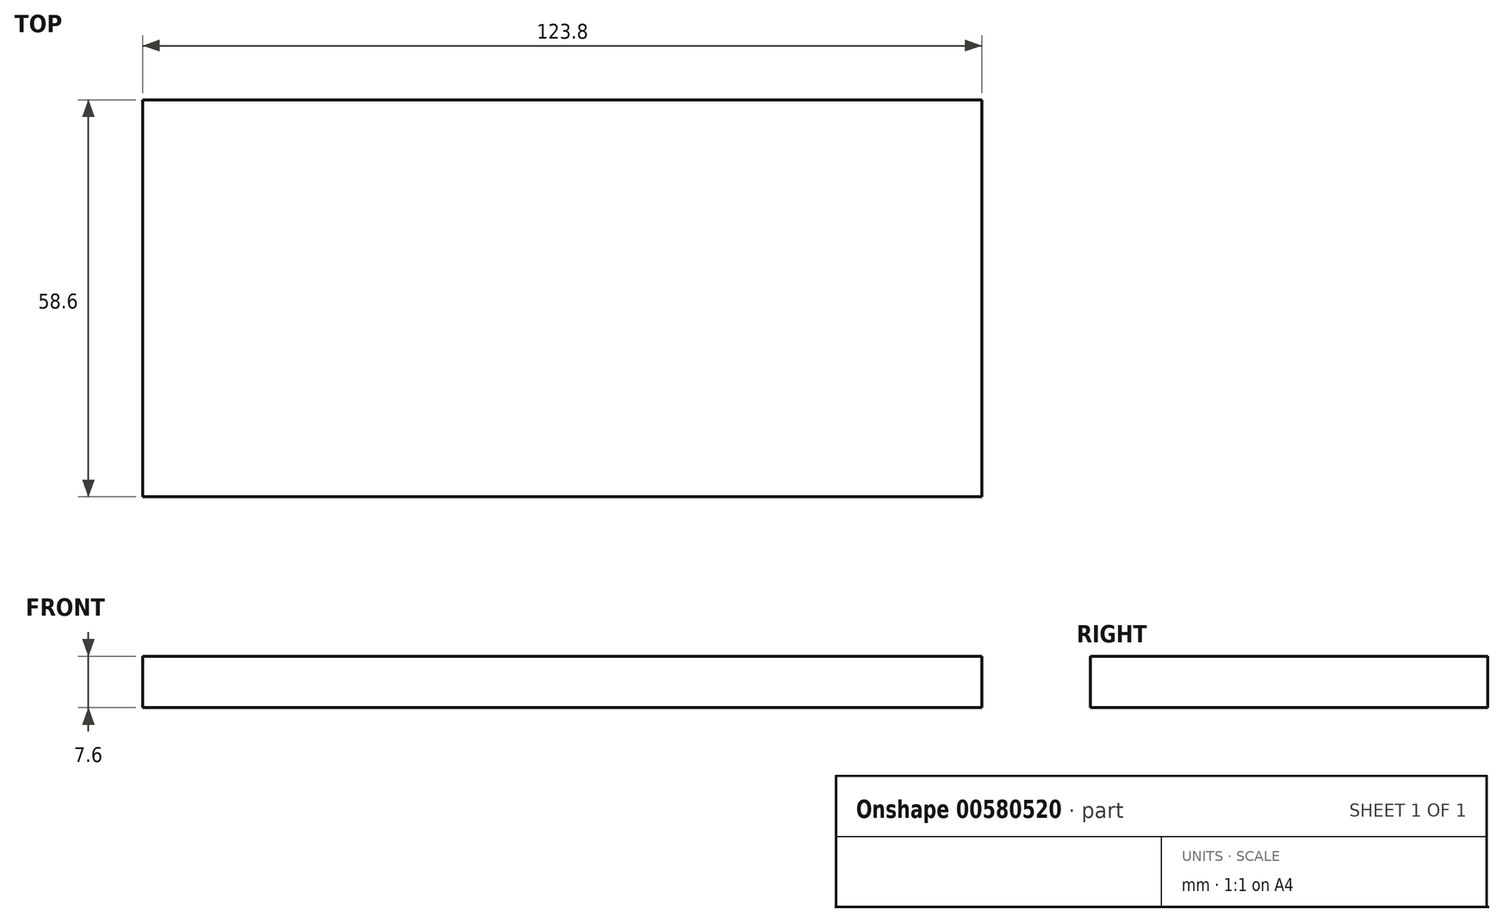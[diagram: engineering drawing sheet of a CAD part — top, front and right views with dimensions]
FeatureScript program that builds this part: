
annotation { "Feature Type Name" : "Feature", "Feature Type Description" : "" }
export const myFeature = defineFeature(function(context is Context, id is Id, definition is map)
    precondition{}
    {
        {
            var Q0;
            Q0=qCreatedBy(makeId("Top.planeOp"),FACE);
            var sketch = newSketch(context, id + "F0", { "sketchPlane" : qUnion([Q0])});
            skLineSegment(sketch, "E0.bottom", {"start": v(-47, 43.9) * mm, "end": v(76.8, 43.9) * mm});
            skLineSegment(sketch, "E0.top", {"start": v(-47, -14.7) * mm, "end": v(76.8, -14.7) * mm});
            skLineSegment(sketch, "E0.left", {"start": v(-47, 43.9) * mm, "end": v(-47, -14.7) * mm});
            skLineSegment(sketch, "E0.right", {"start": v(76.8, 43.9) * mm, "end": v(76.8, -14.7) * mm});
            skSolve(sketch);
        }
        {
            var Q0;
            Q0=makeQuery(id+"F0.imprint","IMPRINT",FACE,{"disambiguationData":[TD([[makeQuery(id+"F0.imprint","IMPRINT",EDGE,{"derivedFrom":sQuery(id+"F0.wireOp",EDGE,"E0.bottom")}),-1.0]])]});
            extrude(context, id + "F1", {"entities" : qUnion([Q0]), "depth" : 0 * mm, "offsetDistance" : 25 * mm, "hasSecondDirection" : true, "secondDirectionOppositeDirection" : true, "secondDirectionDepth" : 7.6 * mm});
        }
    });
